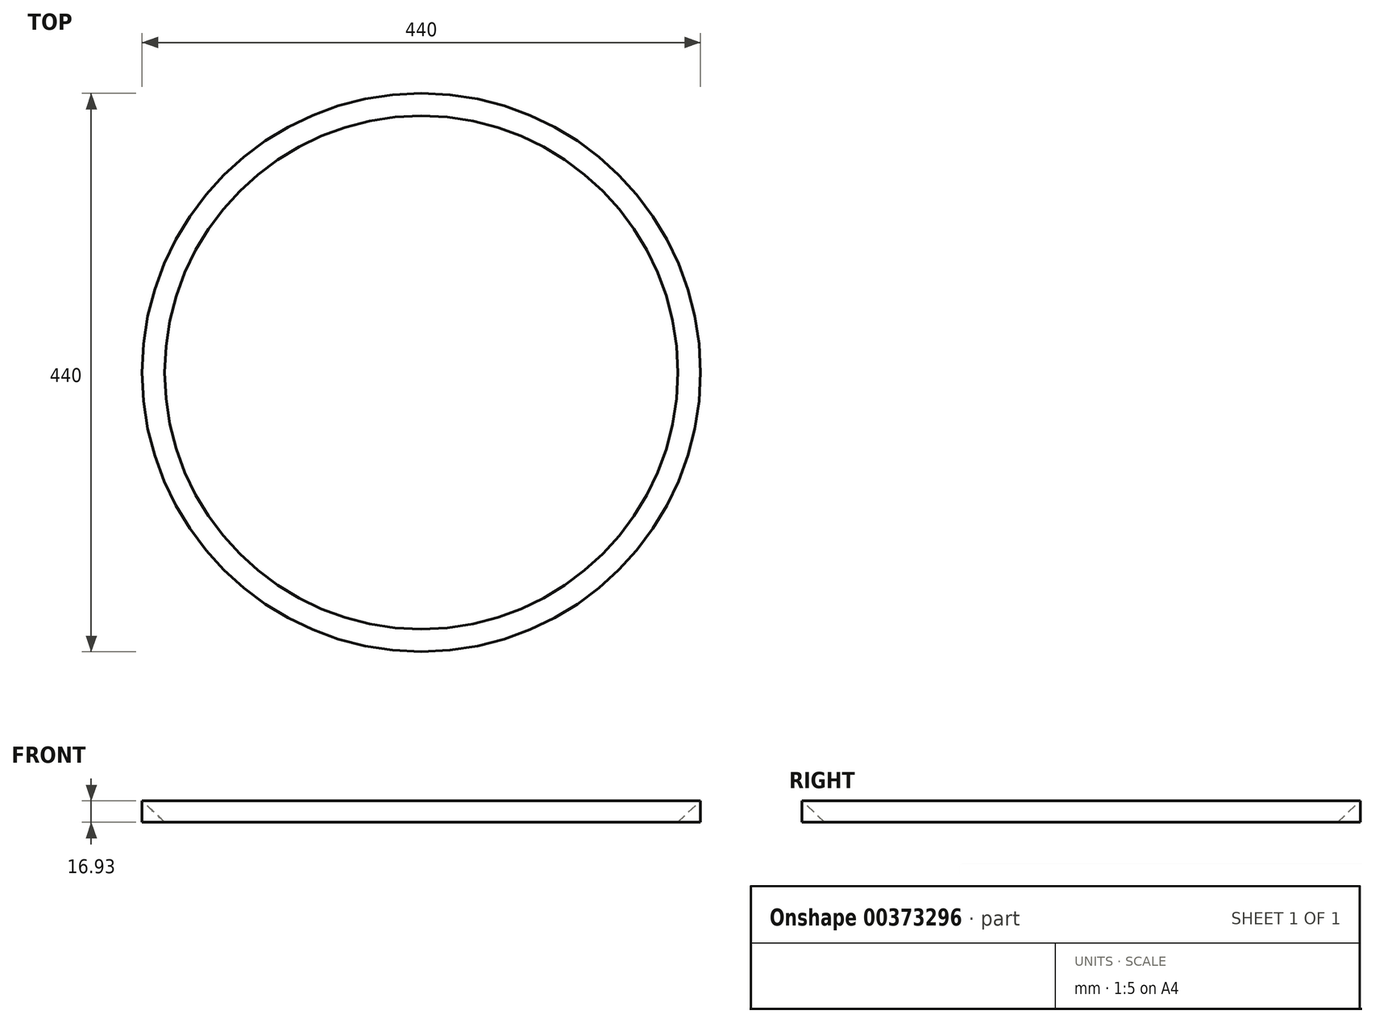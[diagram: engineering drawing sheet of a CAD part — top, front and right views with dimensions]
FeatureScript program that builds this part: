
annotation { "Feature Type Name" : "Feature", "Feature Type Description" : "" }
export const myFeature = defineFeature(function(context is Context, id is Id, definition is map)
    precondition{}
    {
        {
            var Q0;
            Q0=qCreatedBy(makeId("Front.planeOp"),FACE);
            var sketch = newSketch(context, id + "F0", { "sketchPlane" : qUnion([Q0])});
            skLineSegment(sketch, "E0", {"start": v(220, 0) * mm, "end": v(220, 150) * mm});
            skLineSegment(sketch, "E1", {"start": v(220, 150) * mm, "end": v(220, 16.4) * mm});
            skSolve(sketch);
        }
        {
            var Q0;
            Q0=qCreatedBy(makeId("Front.planeOp"),FACE);
            var sketch = newSketch(context, id + "F1", { "sketchPlane" : qUnion([Q0])});
            skLineSegment(sketch, "E2", {"start": v(0, 0) * mm, "end": v(0, 63.28) * mm});
            skSolve(sketch);
        }
        {
            var Q0;
            Q0=qCreatedBy(makeId("Front.planeOp"),FACE);
            var sketch = newSketch(context, id + "F2", { "sketchPlane" : qUnion([Q0])});
            skLineSegment(sketch, "E3", {"start": v(220, 0) * mm, "end": v(202.22, 0) * mm});
            skLineSegment(sketch, "E4", {"start": v(202.22, 0) * mm, "end": v(220, 16.93) * mm});
            skLineSegment(sketch, "E5", {"start": v(220, 16.93) * mm, "end": v(220, 0) * mm});
            skSolve(sketch);
        }
        {
            var Q0;
            Q0=sQuery(id+"F0.wireOp",EDGE,"E0");
            var Q1;
            Q1=sQuery(id+"F1.wireOp",EDGE,"E2");
            revolve(context, id + "F3", {"bodyType" : ToolBodyType.SURFACE, "surfaceEntities" : qUnion([Q0]), "axis" : qUnion([Q1]), "revolveType" : RevolveType.FULL});
        }
        {
            var Q0;
            Q0 = qSketchRegion(id + "F2", true);
            var Q1;
            Q1=sQuery(id+"F1.wireOp",EDGE,"E2");
            revolve(context, id + "F4", {"entities" : qUnion([Q0]), "axis" : qUnion([Q1]), "revolveType" : RevolveType.FULL});
        }
    });
